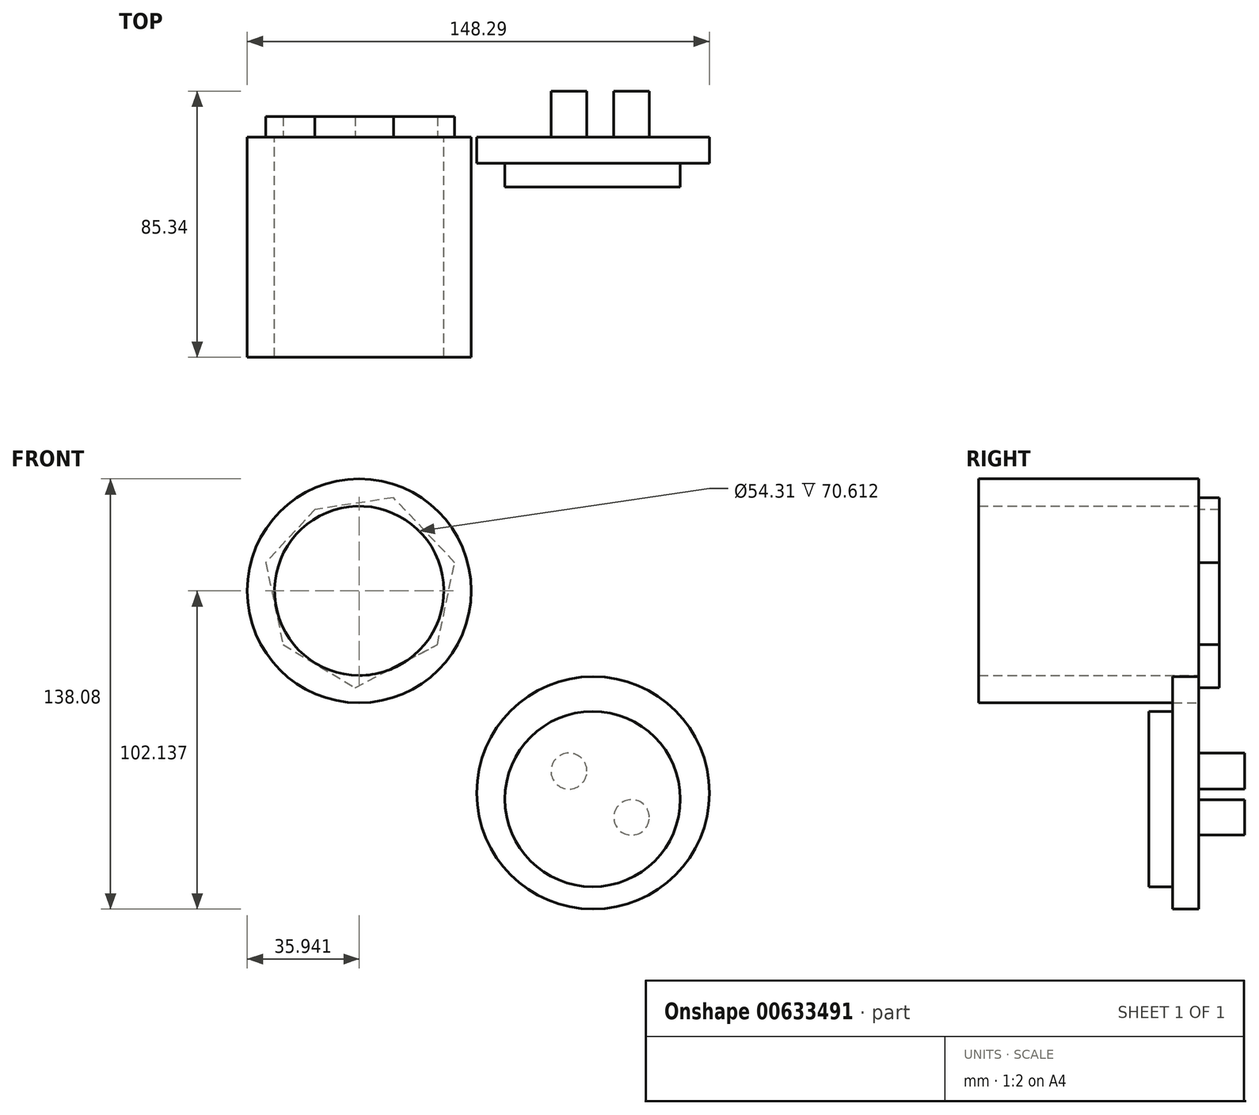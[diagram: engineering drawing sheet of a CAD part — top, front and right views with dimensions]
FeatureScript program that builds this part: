
annotation { "Feature Type Name" : "Feature", "Feature Type Description" : "" }
export const myFeature = defineFeature(function(context is Context, id is Id, definition is map)
    precondition{}
    {
        {
            var Q0;
            Q0=qCreatedBy(makeId("Front.planeOp"),FACE);
            var sketch = newSketch(context, id + "F0", { "sketchPlane" : qUnion([Q0])});
            skCircle(sketch, "E0", {"center": v(-35.17, 37.37) * mm, "radius": 35.94 * mm});
            skCircle(sketch, "E1", {"center": v(-35.17, 37.37) * mm, "radius": 27.16 * mm});
            skSolve(sketch);
        }
        {
            var Q0;
            Q0 = qSketchRegion(id + "F0", true);
            extrude(context, id + "F1", {"entities" : qUnion([Q0]), "depth" : 70.61 * mm, "offsetDistance" : 25.4 * mm});
        }
        {
            var Q0;
            Q0=qCreatedBy(makeId("Front.planeOp"),FACE);
            var sketch = newSketch(context, id + "F2", { "sketchPlane" : qUnion([Q0])});
            skLineSegment(sketch, "E2", {"start": v(-49.38, 63.45) * mm, "end": v(-65.2, 46.45) * mm});
            skLineSegment(sketch, "E3", {"start": v(-65.2, 46.45) * mm, "end": v(-59.63, 20.08) * mm});
            skLineSegment(sketch, "E4", {"start": v(-59.63, 20.08) * mm, "end": v(-36.48, 6.3) * mm});
            skLineSegment(sketch, "E5", {"start": v(-36.48, 6.3) * mm, "end": v(-10.1, 20.08) * mm});
            skLineSegment(sketch, "E6", {"start": v(-10.1, 20.08) * mm, "end": v(-4.53, 46.45) * mm});
            skLineSegment(sketch, "E7", {"start": v(-4.53, 46.45) * mm, "end": v(-24.17, 67.26) * mm});
            skLineSegment(sketch, "E8", {"start": v(-24.17, 67.26) * mm, "end": v(-49.38, 63.45) * mm});
            skSolve(sketch);
        }
        {
            var Q0;
            Q0 = qSketchRegion(id + "F2", true);
            extrude(context, id + "F3", {"entities" : qUnion([Q0]), "operationType" : NewBodyOperationType.ADD, "oppositeDirection" : true, "depth" : 6.6 * mm, "offsetDistance" : 25.4 * mm});
        }
        {
            var Q0;
            Q0=qCreatedBy(makeId("Front.planeOp"),FACE);
            var sketch = newSketch(context, id + "F4", { "sketchPlane" : qUnion([Q0])});
            skPoint(sketch, "E9", {"position": v(-35.6, 74.3) * mm});
            skPoint(sketch, "E10", {"position": v(-35.01, 0) * mm});
            skCircle(sketch, "E11", {"center": v(39.87, -27.45) * mm, "radius": 37.31 * mm});
            skPoint(sketch, "E12", {"position": v(35, 9.54) * mm});
            skPoint(sketch, "E13", {"position": v(37.69, -64.7) * mm});
            skSolve(sketch);
        }
        {
            var Q0;
            Q0 = qSketchRegion(id + "F4", true);
            extrude(context, id + "F5", {"entities" : qUnion([Q0]), "depth" : 8.38 * mm, "offsetDistance" : 25.4 * mm});
        }
        {
            var Q0;
            Q0=qCreatedBy(makeId("Front.planeOp"),FACE);
            var sketch = newSketch(context, id + "F6", { "sketchPlane" : qUnion([Q0])});
            skPoint(sketch, "E14", {"position": v(-35.9, 64.62) * mm});
            skPoint(sketch, "E15", {"position": v(-35.9, 11.28) * mm});
            skPoint(sketch, "E16", {"position": v(36.79, 10.11) * mm});
            skPoint(sketch, "E17", {"position": v(42.36, -64.62) * mm});
            skCircle(sketch, "E18", {"center": v(39.72, -29.45) * mm, "radius": 28.14 * mm});
            skPoint(sketch, "E19", {"position": v(30.03, -3.04) * mm});
            skPoint(sketch, "E20", {"position": v(52.03, -56.38) * mm});
            skSolve(sketch);
        }
        {
            var Q0;
            Q0 = qSketchRegion(id + "F6", true);
            extrude(context, id + "F7", {"entities" : qUnion([Q0]), "operationType" : NewBodyOperationType.ADD, "depth" : 16 * mm, "offsetDistance" : 25.4 * mm});
        }
        {
            var Q0;
            Q0=qCreatedBy(makeId("Front.planeOp"),FACE);
            var sketch = newSketch(context, id + "F8", { "sketchPlane" : qUnion([Q0])});
            skCircle(sketch, "E21", {"center": v(32.12, -20.47) * mm, "radius": 5.77 * mm});
            skCircle(sketch, "E22", {"center": v(52.2, -35.32) * mm, "radius": 5.7 * mm});
            skPoint(sketch, "E23", {"position": v(54.87, -30.29) * mm});
            skPoint(sketch, "E24", {"position": v(49.66, -40.4) * mm});
            skPoint(sketch, "E25", {"position": v(29.33, -15.41) * mm});
            skPoint(sketch, "E26", {"position": v(29.33, -25.52) * mm});
            skSolve(sketch);
        }
        {
            var Q0;
            Q0 = qSketchRegion(id + "F8", true);
            extrude(context, id + "F9", {"entities" : qUnion([Q0]), "operationType" : NewBodyOperationType.ADD, "oppositeDirection" : true, "depth" : 14.73 * mm, "offsetDistance" : 25.4 * mm});
        }
    });
